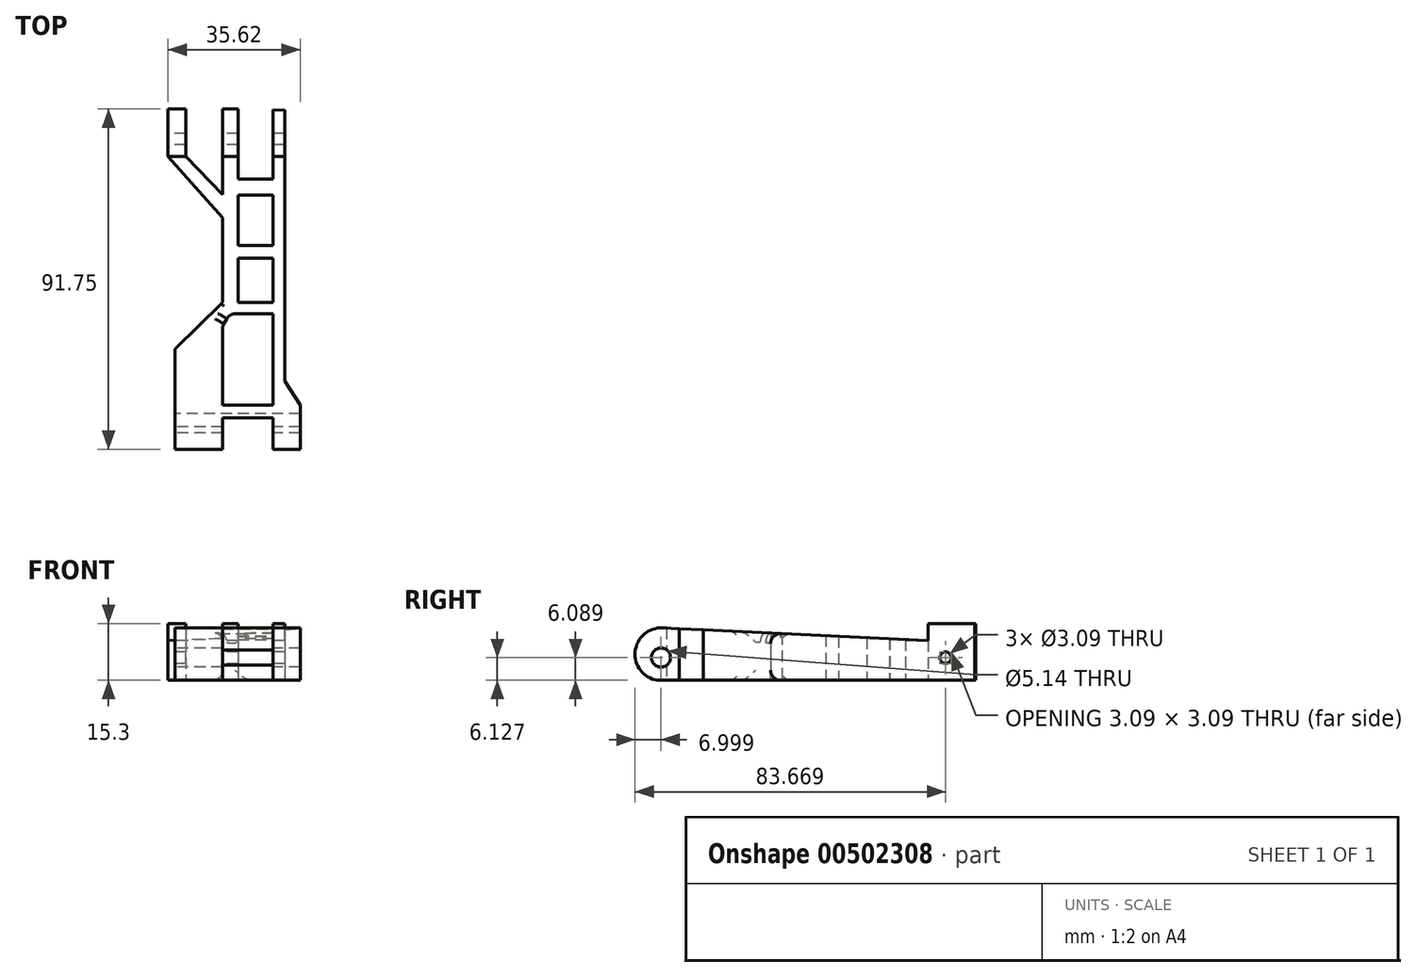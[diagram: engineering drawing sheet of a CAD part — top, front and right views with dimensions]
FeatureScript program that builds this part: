
annotation { "Feature Type Name" : "Feature", "Feature Type Description" : "" }
export const myFeature = defineFeature(function(context is Context, id is Id, definition is map)
    precondition{}
    {
        {
            var Q0;
            Q0=qCreatedBy(makeId("Top.planeOp"),FACE);
            var sketch = newSketch(context, id + "F0", { "sketchPlane" : qUnion([Q0])});
            skLineSegment(sketch, "E0", {"start": v(-43.8, 44.36) * mm, "end": v(-43.8, 25.75) * mm});
            skLineSegment(sketch, "E1", {"start": v(-43.8, -50.72) * mm, "end": v(-36.5, -50.72) * mm});
            skLineSegment(sketch, "E2", {"start": v(-36.5, -50.72) * mm, "end": v(-36.5, -35.22) * mm});
            skLineSegment(sketch, "E3", {"start": v(-40.7, -28.8) * mm, "end": v(-40.7, 44.33) * mm});
            skLineSegment(sketch, "E4", {"start": v(-40.7, 44.33) * mm, "end": v(-43.8, 44.36) * mm});
            skLineSegment(sketch, "E5", {"start": v(-36.5, -35.22) * mm, "end": v(-40.7, -28.8) * mm});
            skLineSegment(sketch, "E6", {"start": v(-43.8, -35.22) * mm, "end": v(-57.44, -35.22) * mm});
            skLineSegment(sketch, "E7", {"start": v(-57.44, -38.61) * mm, "end": v(-57.44, -50.72) * mm});
            skLineSegment(sketch, "E8", {"start": v(-70.28, -50.72) * mm, "end": v(-57.44, -50.72) * mm});
            skLineSegment(sketch, "E9", {"start": v(-70.28, -50.72) * mm, "end": v(-70.28, -20.15) * mm});
            skLineSegment(sketch, "E10", {"start": v(-57.44, -35.22) * mm, "end": v(-57.44, -14) * mm});
            skLineSegment(sketch, "E11", {"start": v(-57.44, -14) * mm, "end": v(-55.55, -10.6) * mm});
            skLineSegment(sketch, "E12", {"start": v(-55.55, -10.6) * mm, "end": v(-43.8, -10.6) * mm});
            skLineSegment(sketch, "E13", {"start": v(-53.26, -7.59) * mm, "end": v(-53.26, 4.34) * mm});
            skLineSegment(sketch, "E14", {"start": v(-53.26, 44.6) * mm, "end": v(-57.44, 44.6) * mm});
            skLineSegment(sketch, "E15", {"start": v(-57.44, 44.6) * mm, "end": v(-57.44, 21.56) * mm});
            skLineSegment(sketch, "E16", {"start": v(-70.28, -20.15) * mm, "end": v(-57.44, -7.59) * mm});
            skPoint(sketch, "E17.end.orphan", {"position": v(-63.3, -7.59) * mm});
            skPoint(sketch, "E18.orphan", {"position": v(-40.7, -35.22) * mm});
            skLineSegment(sketch, "E19", {"start": v(-57.44, 15.3) * mm, "end": v(-72.13, 31.85) * mm});
            skLineSegment(sketch, "E20", {"start": v(-72.13, 31.85) * mm, "end": v(-72.13, 44.6) * mm});
            skLineSegment(sketch, "E21", {"start": v(-72.13, 44.6) * mm, "end": v(-67.32, 44.6) * mm});
            skLineSegment(sketch, "E22", {"start": v(-67.32, 44.6) * mm, "end": v(-67.32, 31.85) * mm});
            skLineSegment(sketch, "E23", {"start": v(-67.32, 31.85) * mm, "end": v(-57.44, 21.56) * mm});
            skLineSegment(sketch, "E24.trimOffspring", {"start": v(-57.44, 15.3) * mm, "end": v(-57.44, -7.59) * mm});
            skPoint(sketch, "E25.start.orphan", {"position": v(-49.67, -10.6) * mm});
            skPoint(sketch, "E26.orphan", {"position": v(-43.8, 1.61) * mm});
            skPoint(sketch, "E27.start.orphan", {"position": v(-53.26, 1.61) * mm});
            skLineSegment(sketch, "E28", {"start": v(-49.67, -7.59) * mm, "end": v(-43.8, -7.59) * mm});
            skLineSegment(sketch, "E29", {"start": v(-43.8, -7.59) * mm, "end": v(-53.26, -7.59) * mm});
            skLineSegment(sketch, "E30.trimOffspring", {"start": v(-43.8, -10.6) * mm, "end": v(-43.8, -35.22) * mm});
            skPoint(sketch, "E31.orphan", {"position": v(-53.26, -10.6) * mm});
            skLineSegment(sketch, "E32", {"start": v(-49.67, 4.34) * mm, "end": v(-53.26, 4.34) * mm});
            skLineSegment(sketch, "E33", {"start": v(-53.26, 4.34) * mm, "end": v(-43.8, 4.34) * mm});
            skPoint(sketch, "E34.endSnap0", {"position": v(-40.7, 7.76) * mm});
            skLineSegment(sketch, "E35", {"start": v(-43.8, 7.76) * mm, "end": v(-53.26, 7.76) * mm});
            skLineSegment(sketch, "E36", {"start": v(-53.26, 7.76) * mm, "end": v(-53.26, 21.43) * mm});
            skLineSegment(sketch, "E37", {"start": v(-53.26, 21.43) * mm, "end": v(-43.8, 21.43) * mm});
            skLineSegment(sketch, "E38", {"start": v(-43.8, 25.75) * mm, "end": v(-53.26, 25.75) * mm});
            skLineSegment(sketch, "E39.trimOffspring", {"start": v(-53.26, 25.75) * mm, "end": v(-53.26, 44.6) * mm});
            skLineSegment(sketch, "E40.trimOffspring", {"start": v(-43.8, 21.43) * mm, "end": v(-43.8, 7.76) * mm});
            skLineSegment(sketch, "E41.trimOffspring", {"start": v(-43.8, 4.34) * mm, "end": v(-43.8, -7.59) * mm});
            skLineSegment(sketch, "E42", {"start": v(-57.44, -38.61) * mm, "end": v(-43.8, -38.61) * mm});
            skLineSegment(sketch, "E43.trimOffspring", {"start": v(-43.8, -38.61) * mm, "end": v(-43.8, -50.72) * mm});
            skSolve(sketch);
        }
        {
            var Q0;
            Q0 = qSketchRegion(id + "F0", true);
            extrude(context, id + "F1", {"entities" : qUnion([Q0]), "depth" : 15.3 * mm});
        }
        {
            var Q0;
            Q0=makeQuery(id+"F1.opExtrude","SWEPT_FACE",FACE,{"disambiguationData":[OSD([sQuery(id+"F0.wireOp",EDGE,"E20")])]});
            var sketch = newSketch(context, id + "F2", { "sketchPlane" : qUnion([Q0])});
            skPoint(sketch, "E44.orphan", {"position": v(-38.23, 0) * mm});
            skCircle(sketch, "E45", {"center": v(-38.23, 5.13) * mm, "radius": 2.47 * mm});
            skPoint(sketch, "E46.orphan", {"position": v(-38.23, 2.66) * mm});
            skPoint(sketch, "E47.end.orphan", {"position": v(-38.23, 7.6) * mm});
            skPoint(sketch, "E48.orphan", {"position": v(40.05, 5.44) * mm});
            skPoint(sketch, "E49.start.orphan", {"position": v(40.05, 0) * mm});
            skPoint(sketch, "E50.start.orphan", {"position": v(40.05, 10.89) * mm});
            skPoint(sketch, "E51.center.orphan", {"position": v(40.05, 8.16) * mm});
            skCircle(sketch, "E52", {"center": v(40.03, 7.03) * mm, "radius": 7.12 * mm});
            skCircle(sketch, "E53", {"center": v(-38.23, 5.13) * mm, "radius": 5.24 * mm});
            skLineSegment(sketch, "E54", {"start": v(40.05, 0) * mm, "end": v(-38.23, 0) * mm});
            skLineSegment(sketch, "E55", {"start": v(-38.23, 10.37) * mm, "end": v(40.05, 14.16) * mm});
            skLineSegment(sketch, "E56.bottom", {"start": v(-50.8, 17.87) * mm, "end": v(58.34, 17.87) * mm});
            skLineSegment(sketch, "E56.top", {"start": v(-50.8, -4.66) * mm, "end": v(58.34, -4.66) * mm});
            skLineSegment(sketch, "E56.left", {"start": v(-50.8, 17.87) * mm, "end": v(-50.8, -4.66) * mm});
            skLineSegment(sketch, "E56.right", {"start": v(58.34, 17.87) * mm, "end": v(58.34, -4.66) * mm});
            skCircle(sketch, "E57", {"center": v(40.03, 7.03) * mm, "radius": 2.75 * mm});
            skSolve(sketch);
        }
        {
            var Q0;
            Q0=makeQuery(id+"F2.imprint","IMPRINT",FACE,{"disambiguationData":[TD([[makeQuery(id+"F2.imprint","IMPRINT",EDGE,{"derivedFrom":sQuery(id+"F2.wireOp",EDGE,"E56.bottom")}),-1.0]])]});
            extrude(context, id + "F3", {"entities" : qUnion([Q0]), "operationType" : NewBodyOperationType.REMOVE, "oppositeDirection" : true, "depth" : 77 * mm});
        }
        {
            var Q0;
            Q0=makeQuery(id+"F1.opExtrude","SWEPT_FACE",FACE,{"disambiguationData":[OSD([sQuery(id+"F0.wireOp",EDGE,"E20")])]});
            var sketch = newSketch(context, id + "F4", { "sketchPlane" : qUnion([Q0])});
            skCircle(sketch, "E58", {"center": v(40.14, 6.13) * mm, "radius": 2.57 * mm});
            skSolve(sketch);
        }
        {
            var Q0;
            Q0 = qSketchRegion(id + "F4", true);
            extrude(context, id + "F5", {"entities" : qUnion([Q0]), "operationType" : NewBodyOperationType.REMOVE, "oppositeDirection" : true, "depth" : 65.4 * mm});
        }
        {
            var Q0;
            Q0=makeQuery(id+"F1.opExtrude","SWEPT_FACE",FACE,{"disambiguationData":[OSD([sQuery(id+"F0.wireOp",EDGE,"E20")])]});
            var sketch = newSketch(context, id + "F6", { "sketchPlane" : qUnion([Q0])});
            skCircle(sketch, "E59", {"center": v(-36.53, 6.09) * mm, "radius": 1.55 * mm});
            skSolve(sketch);
        }
        {
            var Q0;
            Q0 = qSketchRegion(id + "F6", true);
            extrude(context, id + "F7", {"entities" : qUnion([Q0]), "operationType" : NewBodyOperationType.REMOVE, "oppositeDirection" : true, "depth" : 54.6 * mm});
        }
        {
            var Q0;
            Q0=makeQuery(id+"F1.opExtrude","SWEPT_FACE",FACE,{"disambiguationData":[OSD([sQuery(id+"F0.wireOp",EDGE,"E11")])]});
            fillet(context, id + "F8", {"entities" : qUnion([Q0]), "radius" : 2.66 * mm, "tangentPropagation" : true, "allowEdgeOverflow" : false});
        }
        {
            var Q0;
            Q0=makeQuery(id+"F1.opExtrude","SWEPT_FACE",FACE,{"disambiguationData":[OSD([sQuery(id+"F0.wireOp",EDGE,"E16")])]});
            fillet(context, id + "F9", {"entities" : qUnion([Q0]), "radius" : 1 * mm, "tangentPropagation" : true, "allowEdgeOverflow" : false});
        }
        {
            var Q0;
            Q0=makeQuery(id+"F1.opExtrude","SWEPT_FACE",FACE,{"disambiguationData":[OSD([sQuery(id+"F0.wireOp",EDGE,"E4")])]});
            fillet(context, id + "F10", {"entities" : qUnion([Q0]), "radius" : 0.02 * mm, "tangentPropagation" : true, "allowEdgeOverflow" : false});
        }
    });
